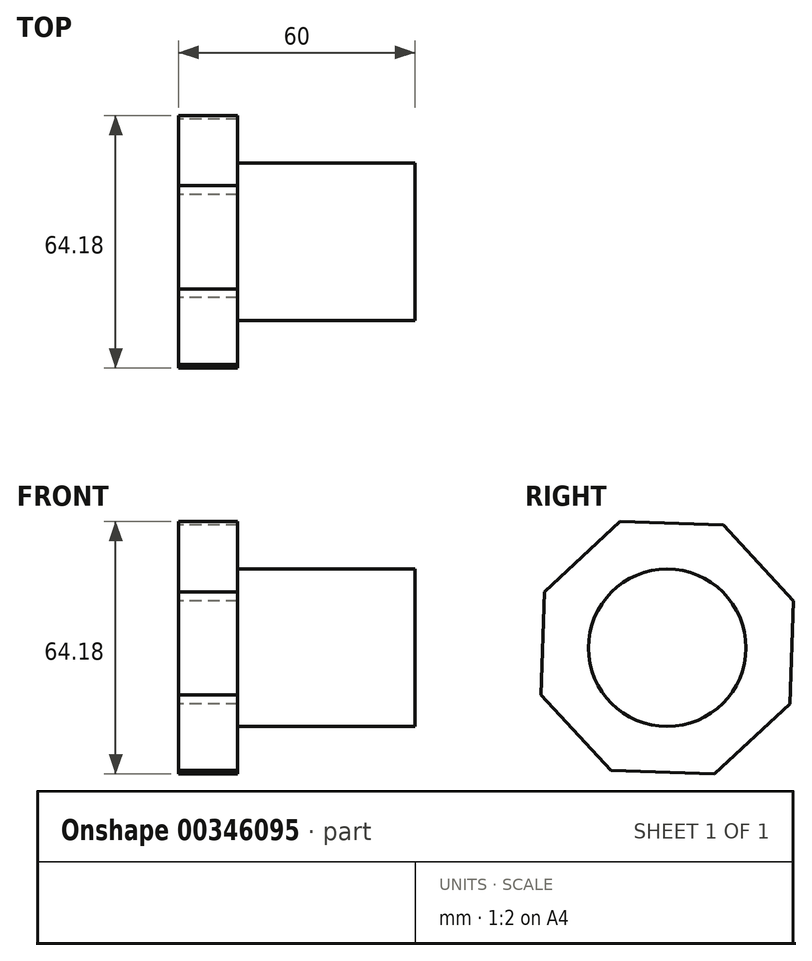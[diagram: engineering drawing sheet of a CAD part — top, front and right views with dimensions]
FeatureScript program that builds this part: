
annotation { "Feature Type Name" : "Feature", "Feature Type Description" : "" }
export const myFeature = defineFeature(function(context is Context, id is Id, definition is map)
    precondition{}
    {
        {
            var Q0;
            Q0=qCreatedBy(makeId("Front.planeOp"),FACE);
            var sketch = newSketch(context, id + "F0", { "sketchPlane" : qUnion([Q0])});
            skLineSegment(sketch, "E0", {"start": v(0, 0) * mm, "end": v(45, 0) * mm});
            skLineSegment(sketch, "E1", {"start": v(45, 0) * mm, "end": v(45, 20) * mm});
            skLineSegment(sketch, "E2", {"start": v(45, 20) * mm, "end": v(0, 20) * mm});
            skLineSegment(sketch, "E3", {"start": v(0, 20) * mm, "end": v(0, 0) * mm});
            skLineSegment(sketch, "E4.bottom", {"start": v(0, 0) * mm, "end": v(-15, 0) * mm});
            skLineSegment(sketch, "E4.top", {"start": v(0, 40) * mm, "end": v(-15, 40) * mm});
            skLineSegment(sketch, "E4.left", {"start": v(0, 0) * mm, "end": v(0, 40) * mm});
            skLineSegment(sketch, "E4.right", {"start": v(-15, 0) * mm, "end": v(-15, 40) * mm});
            skLineSegment(sketch, "E5", {"start": v(-57.56, 0) * mm, "end": v(68.6, 0) * mm, "construction": true});
            skSolve(sketch);
        }
        {
            var Q0;
            Q0 = qSketchRegion(id + "F0", true);
            var Q1;
            Q1=sQuery(id+"F0.wireOp",EDGE,"E5");
            revolve(context, id + "F1", {"entities" : qUnion([Q0]), "axis" : qUnion([Q1]), "revolveType" : RevolveType.FULL});
        }
        {
            var Q0;
            Q0=makeQuery(id+"F1.opRevolve","SWEPT_FACE",FACE,{"disambiguationData":[OSD([sQuery(id+"F0.wireOp",EDGE,"E4.right")])]});
            var sketch = newSketch(context, id + "F2", { "sketchPlane" : qUnion([Q0])});
            skCircle(sketch, "E6.cCircle", {"center": v(0, 0) * mm, "radius": 31.64 * mm, "construction": true});
            skLineSegment(sketch, "E6.0", {"start": v(11.96, 32.1) * mm, "end": v(31.15, 14.23) * mm});
            skLineSegment(sketch, "E6.1", {"start": v(31.15, 14.23) * mm, "end": v(32.1, -11.96) * mm});
            skLineSegment(sketch, "E6.2", {"start": v(32.1, -11.96) * mm, "end": v(14.23, -31.15) * mm});
            skLineSegment(sketch, "E6.3", {"start": v(14.23, -31.15) * mm, "end": v(-11.96, -32.1) * mm});
            skLineSegment(sketch, "E6.4", {"start": v(-11.96, -32.1) * mm, "end": v(-31.15, -14.23) * mm});
            skLineSegment(sketch, "E6.5", {"start": v(-31.15, -14.23) * mm, "end": v(-32.1, 11.96) * mm});
            skLineSegment(sketch, "E6.6", {"start": v(-32.1, 11.96) * mm, "end": v(-14.23, 31.15) * mm});
            skLineSegment(sketch, "E6.7", {"start": v(-14.23, 31.15) * mm, "end": v(11.96, 32.1) * mm});
            skPoint(sketch, "E6.0.midPoint", {"position": v(21.56, 23.16) * mm});
            skCircle(sketch, "E7.0", {"center": v(0, 0) * mm, "radius": 40 * mm});
            skSolve(sketch);
        }
        {
            var Q0;
            Q0=makeQuery(id+"F2.imprint","IMPRINT",FACE,{"disambiguationData":[TD([[makeQuery(id+"F2.imprint","IMPRINT",EDGE,{"derivedFrom":sQuery(id+"F2.wireOp",EDGE,"E6.0")}),1.0]])]});
            extrude(context, id + "F3", {"entities" : qUnion([Q0]), "operationType" : NewBodyOperationType.REMOVE, "oppositeDirection" : true, "depth" : 25 * mm});
        }
    });
